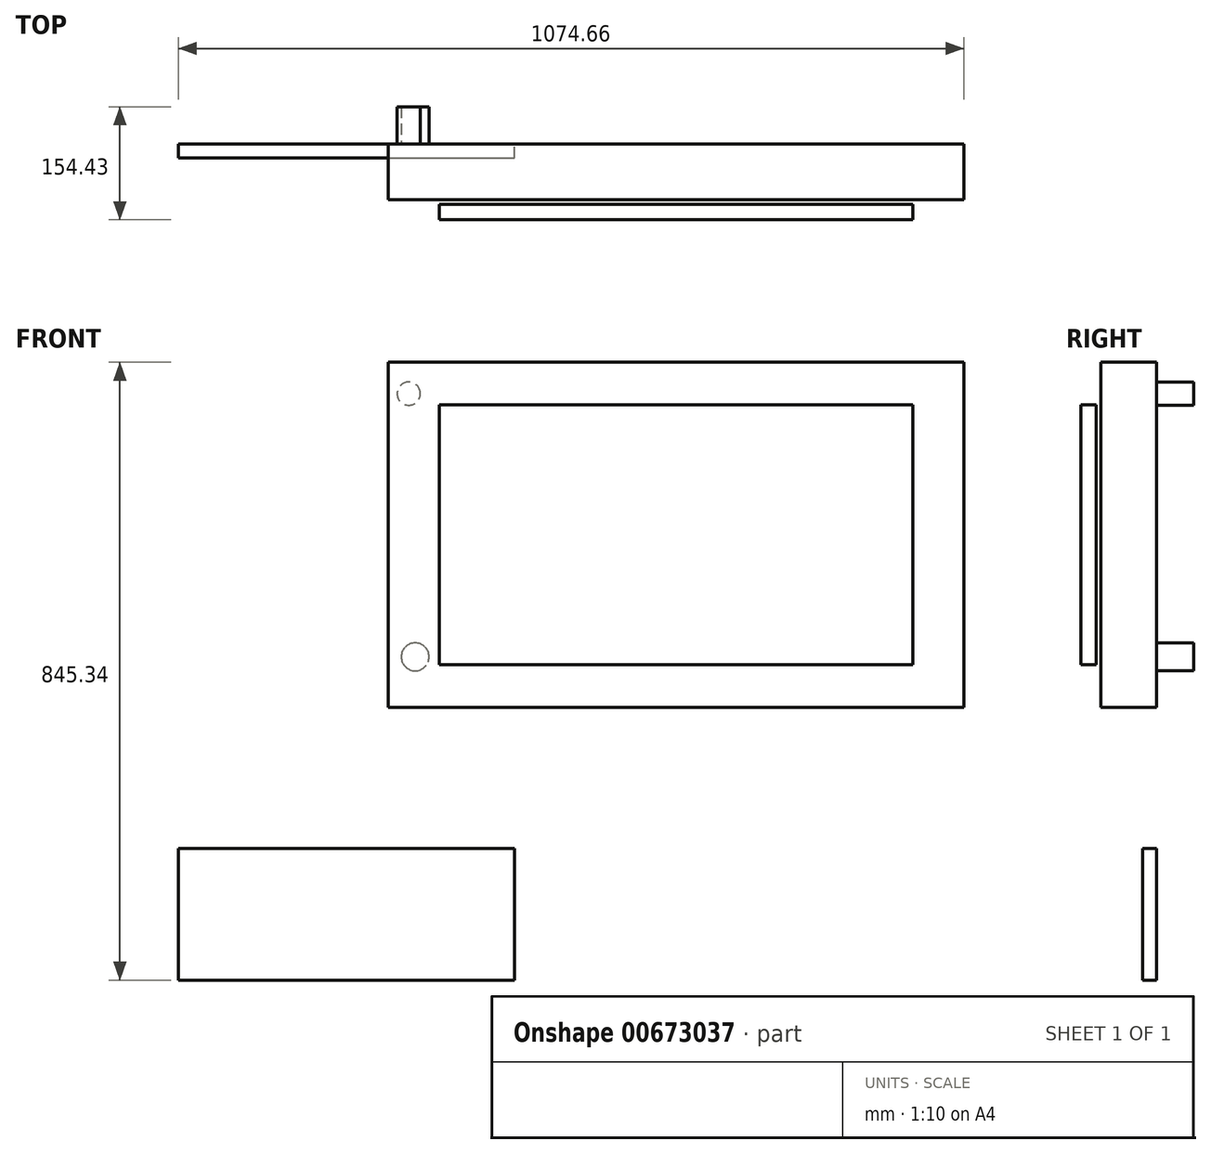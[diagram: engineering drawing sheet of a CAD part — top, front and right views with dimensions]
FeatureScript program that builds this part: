
annotation { "Feature Type Name" : "Feature", "Feature Type Description" : "" }
export const myFeature = defineFeature(function(context is Context, id is Id, definition is map)
    precondition{}
    {
        {
            var Q0;
            Q0=qCreatedBy(makeId("Front.planeOp"),FACE);
            var sketch = newSketch(context, id + "F0", { "sketchPlane" : qUnion([Q0])});
            skLineSegment(sketch, "E0.bottom", {"start": v(0, 0) * mm, "end": v(787.4, 0) * mm});
            skLineSegment(sketch, "E0.top", {"start": v(0, -472.44) * mm, "end": v(787.4, -472.44) * mm});
            skLineSegment(sketch, "E0.left", {"start": v(0, 0) * mm, "end": v(0, -472.44) * mm});
            skLineSegment(sketch, "E0.right", {"start": v(787.4, 0) * mm, "end": v(787.4, -472.44) * mm});
            skSolve(sketch);
        }
        {
            var Q0;
            Q0 = qSketchRegion(id + "F0", true);
            extrude(context, id + "F1", {"entities" : qUnion([Q0]), "depth" : 76.2 * mm, "offsetDistance" : 25.4 * mm});
        }
        {
            var Q0;
            Q0=makeQuery(id+"F1.opExtrude","CAP_FACE",FACE,{"disambiguationData":[OSD([sQuery(id+"F0.wireOp",EDGE,"E0.bottom"),sQuery(id+"F0.wireOp",EDGE,"E0.top"),sQuery(id+"F0.wireOp",EDGE,"E0.left"),sQuery(id+"F0.wireOp",EDGE,"E0.right")])],"isStart":false});
            var sketch = newSketch(context, id + "F2", { "sketchPlane" : qUnion([Q0])});
            skLineSegment(sketch, "E1", {"start": v(0, 0) * mm, "end": v(69.85, 0) * mm, "construction": true});
            skLineSegment(sketch, "E2", {"start": v(69.85, 0) * mm, "end": v(69.85, -58.42) * mm, "construction": true});
            skLineSegment(sketch, "E3.bottom", {"start": v(69.85, -58.42) * mm, "end": v(717.55, -58.42) * mm});
            skLineSegment(sketch, "E3.top", {"start": v(69.85, -414.02) * mm, "end": v(717.55, -414.02) * mm});
            skLineSegment(sketch, "E3.left", {"start": v(69.85, -58.42) * mm, "end": v(69.85, -414.02) * mm});
            skLineSegment(sketch, "E3.right", {"start": v(717.55, -58.42) * mm, "end": v(717.55, -414.02) * mm});
            skSolve(sketch);
        }
        {
            var Q0;
            Q0 = qSketchRegion(id + "F2", true);
            extrude(context, id + "F3", {"entities" : qUnion([Q0]), "depth" : 21.08 * mm, "offsetDistance" : 25.4 * mm});
        }
        {
            var Q0;
            Q0=makeQuery(id+"F3.opExtrude","SWEPT_BODY",BODY,{"disambiguationData":[OSD([sQuery(id+"F2.wireOp",EDGE,"E3.bottom"),sQuery(id+"F2.wireOp",EDGE,"E3.top"),sQuery(id+"F2.wireOp",EDGE,"E3.left"),sQuery(id+"F2.wireOp",EDGE,"E3.right")])]});
            transform(context, id + "F4", {"entities" : qUnion([Q0]), "transformType" : TransformType.TRANSLATION_3D, "dx" : 0 * mm, "dy" : -6.35 * mm, "dz" : 0 * mm, "makeCopy" : false});
        }
        {
            var Q0;
            Q0=makeQuery(id+"F1.opExtrude","CAP_FACE",FACE,{"disambiguationData":[OSD([sQuery(id+"F0.wireOp",EDGE,"E0.bottom"),sQuery(id+"F0.wireOp",EDGE,"E0.top"),sQuery(id+"F0.wireOp",EDGE,"E0.left"),sQuery(id+"F0.wireOp",EDGE,"E0.right")])],"isStart":true});
            var sketch = newSketch(context, id + "F5", { "sketchPlane" : qUnion([Q0])});
            skCircle(sketch, "E4", {"center": v(-28.04, -42.94) * mm, "radius": 15.88 * mm});
            skCircle(sketch, "E5", {"center": v(-36.82, -403.08) * mm, "radius": 19.05 * mm});
            skSolve(sketch);
        }
        {
            var Q0;
            Q0=makeQuery(id+"F5.imprint","IMPRINT",FACE,{"disambiguationData":[TD([[makeQuery(id+"F5.imprint","IMPRINT",EDGE,{"derivedFrom":sQuery(id+"F5.wireOp",EDGE,"E5")}),1.0]])]});
            var Q1;
            Q1=makeQuery(id+"F5.imprint","IMPRINT",FACE,{"disambiguationData":[TD([[makeQuery(id+"F5.imprint","IMPRINT",EDGE,{"derivedFrom":sQuery(id+"F5.wireOp",EDGE,"E4")}),1.0]])]});
            extrude(context, id + "F6", {"entities" : qUnion([Q0, Q1]), "operationType" : NewBodyOperationType.ADD, "depth" : 50.8 * mm, "offsetDistance" : 25.4 * mm});
        }
        {
            var Q0;
            Q0=qCreatedBy(makeId("Front.planeOp"),FACE);
            var sketch = newSketch(context, id + "F7", { "sketchPlane" : qUnion([Q0])});
            skLineSegment(sketch, "E6.bottom", {"start": v(-287.26, -665) * mm, "end": v(172.48, -665) * mm});
            skLineSegment(sketch, "E6.top", {"start": v(-287.26, -845.34) * mm, "end": v(172.48, -845.34) * mm});
            skLineSegment(sketch, "E6.left", {"start": v(-287.26, -665) * mm, "end": v(-287.26, -845.34) * mm});
            skLineSegment(sketch, "E6.right", {"start": v(172.48, -665) * mm, "end": v(172.48, -845.34) * mm});
            skSolve(sketch);
        }
        {
            var Q0;
            Q0 = qSketchRegion(id + "F7", true);
            extrude(context, id + "F8", {"entities" : qUnion([Q0]), "depth" : 19.05 * mm, "offsetDistance" : 25.4 * mm});
        }
    });
